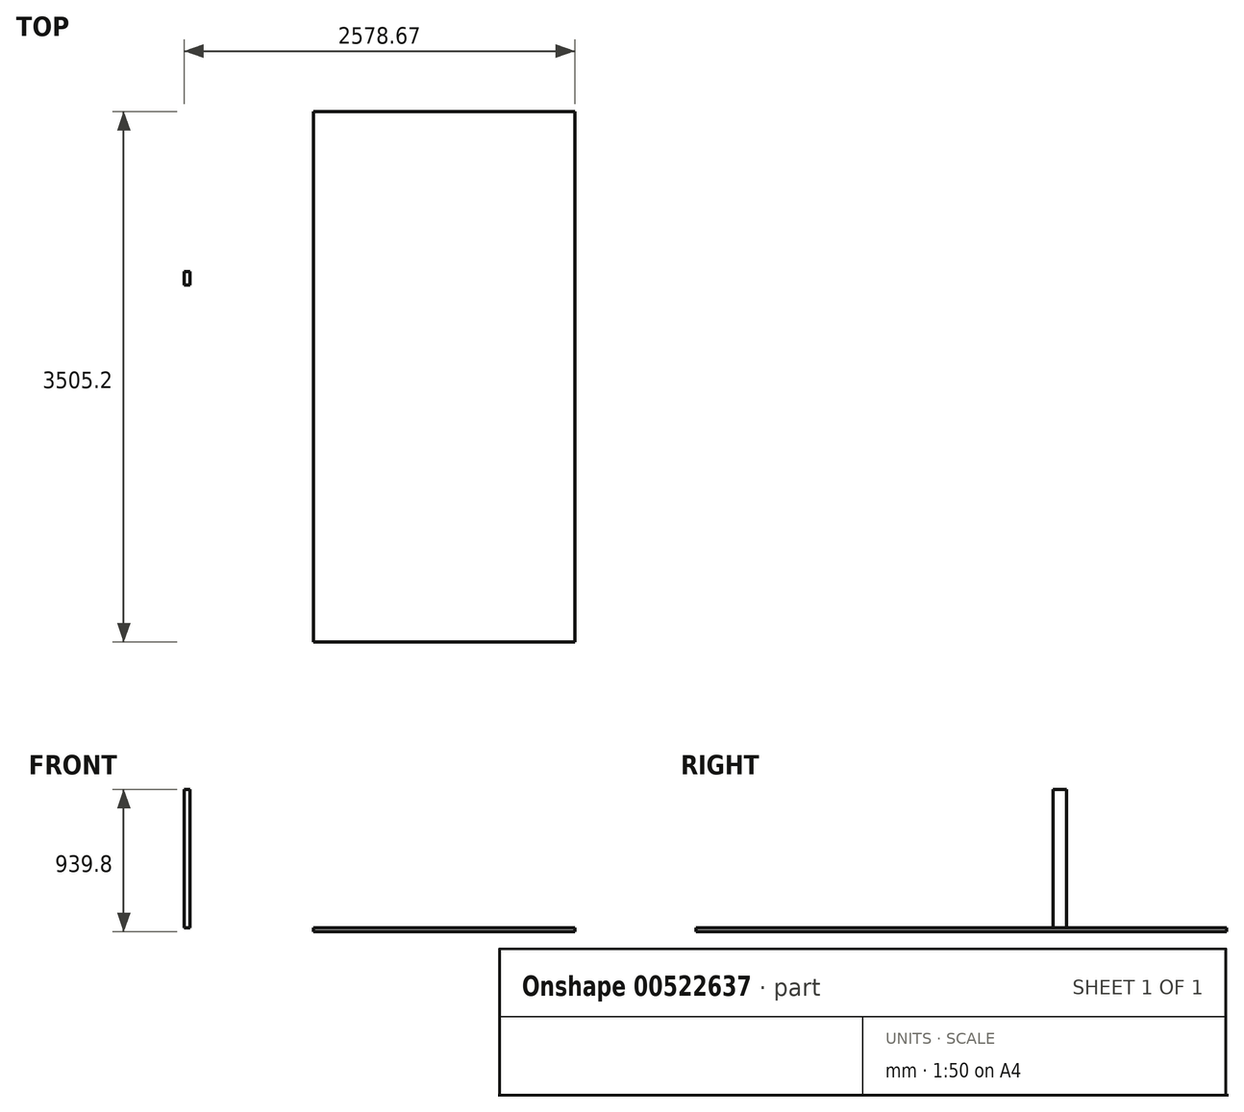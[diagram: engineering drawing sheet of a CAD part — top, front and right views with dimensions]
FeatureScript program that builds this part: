
annotation { "Feature Type Name" : "Feature", "Feature Type Description" : "" }
export const myFeature = defineFeature(function(context is Context, id is Id, definition is map)
    precondition{}
    {
        {
            var Q0;
            Q0=qCreatedBy(makeId("Top.planeOp"),FACE);
            var sketch = newSketch(context, id + "F0", { "sketchPlane" : qUnion([Q0])});
            skLineSegment(sketch, "E0.bottom", {"start": v(-1938.66, 1754.65) * mm, "end": v(-211.46, 1754.65) * mm});
            skLineSegment(sketch, "E0.top", {"start": v(-1938.66, -1750.55) * mm, "end": v(-211.46, -1750.55) * mm});
            skLineSegment(sketch, "E0.left", {"start": v(-1938.66, 1754.65) * mm, "end": v(-1938.66, -1750.55) * mm});
            skLineSegment(sketch, "E0.right", {"start": v(-211.46, 1754.65) * mm, "end": v(-211.46, -1750.55) * mm});
            skSolve(sketch);
        }
        {
            var Q0;
            Q0 = qSketchRegion(id + "F0", true);
            extrude(context, id + "F1", {"entities" : qUnion([Q0]), "depth" : 25.4 * mm, "offsetDistance" : 25.4 * mm});
        }
        {
            var Q0;
            Q0=makeQuery(id+"F1.opExtrude","CAP_FACE",FACE,{"disambiguationData":[OSD([sQuery(id+"F0.wireOp",EDGE,"E0.bottom"),sQuery(id+"F0.wireOp",EDGE,"E0.top"),sQuery(id+"F0.wireOp",EDGE,"E0.left"),sQuery(id+"F0.wireOp",EDGE,"E0.right")])],"isStart":false});
            var sketch = newSketch(context, id + "F2", { "sketchPlane" : qUnion([Q0])});
            skLineSegment(sketch, "E1.bottom", {"start": v(-2790.13, 697.78) * mm, "end": v(-2752.03, 697.78) * mm});
            skLineSegment(sketch, "E1.top", {"start": v(-2790.13, 608.88) * mm, "end": v(-2752.03, 608.88) * mm});
            skLineSegment(sketch, "E1.left", {"start": v(-2790.13, 697.78) * mm, "end": v(-2790.13, 608.88) * mm});
            skLineSegment(sketch, "E1.right", {"start": v(-2752.03, 697.78) * mm, "end": v(-2752.03, 608.88) * mm});
            skSolve(sketch);
        }
        {
            var Q0;
            Q0=makeQuery(id+"F2.imprint","IMPRINT",FACE,{"disambiguationData":[TD([[makeQuery(id+"F2.imprint","IMPRINT",EDGE,{"derivedFrom":sQuery(id+"F2.wireOp",EDGE,"E1.bottom")}),-1.0]])]});
            extrude(context, id + "F3", {"entities" : qUnion([Q0]), "depth" : 914.4 * mm, "offsetDistance" : 25.4 * mm});
        }
    });
